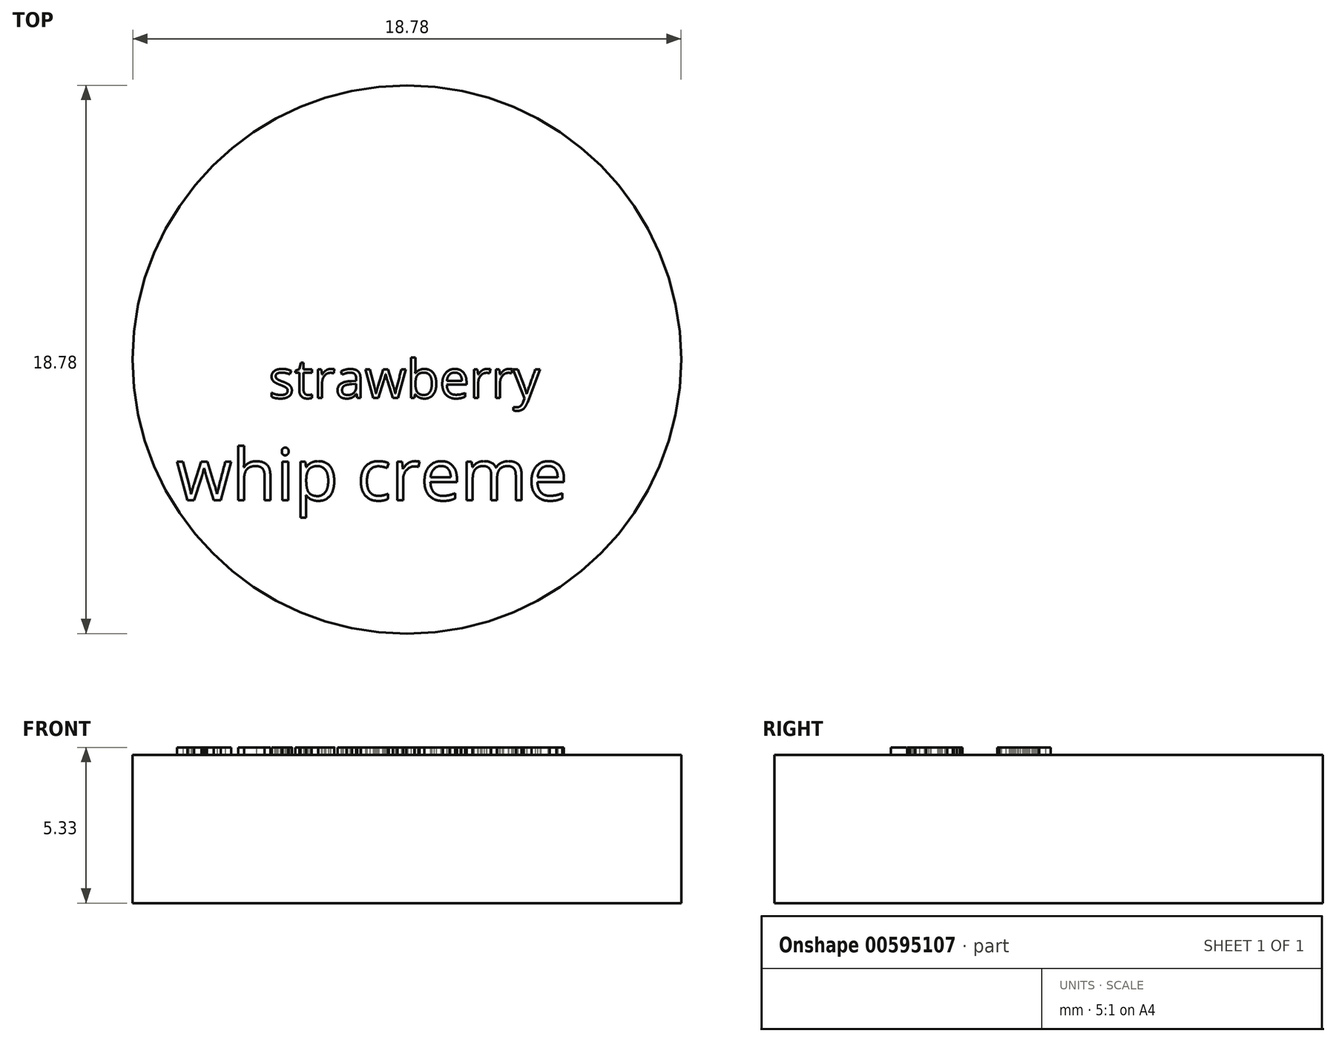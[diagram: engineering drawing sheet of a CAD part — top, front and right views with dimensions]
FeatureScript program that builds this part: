
annotation { "Feature Type Name" : "Feature", "Feature Type Description" : "" }
export const myFeature = defineFeature(function(context is Context, id is Id, definition is map)
    precondition{}
    {
        {
            var Q0;
            Q0=qCreatedBy(makeId("Top.planeOp"),FACE);
            var sketch = newSketch(context, id + "F0", { "sketchPlane" : qUnion([Q0])});
            skCircle(sketch, "E0", {"center": v(0, 0) * mm, "radius": 9.4 * mm});
            skSolve(sketch);
        }
        {
            var Q0;
            Q0=makeQuery(id+"F0.imprint","IMPRINT",FACE,{"disambiguationData":[TD([[makeQuery(id+"F0.imprint","IMPRINT",EDGE,{"derivedFrom":sQuery(id+"F0.wireOp",EDGE,"E0")}),1.0]])]});
            extrude(context, id + "F1", {"entities" : qUnion([Q0]), "oppositeDirection" : true, "depth" : 5.08 * mm, "offsetDistance" : 25.4 * mm});
        }
        {
            var Q0;
            Q0=makeQuery(id+"F1.opExtrude","CAP_FACE",FACE,{"disambiguationData":[OSD([sQuery(id+"F0.wireOp",EDGE,"E0")])],"isStart":true});
            var sketch = newSketch(context, id + "F2", { "sketchPlane" : qUnion([Q0])});
            skText(sketch, "E1", { "text": "strawberry", "fontName": "OpenSans-Regular.ttf"});
            const initialGuessF2  = {"E1": [-0.00473, -0.00132, 1, 0, 0.00132]};
            skSetInitialGuess(sketch, initialGuessF2);
            skSolve(sketch);
        }
        {
            var Q0;
            Q0=makeQuery(id+"F2.imprint","IMPRINT",FACE,{"disambiguationData":[TD([[makeQuery(id+"F2.imprint","IMPRINT",EDGE,{"derivedFrom":sQuery(id+"F2.wireOp",EDGE,"E1.sketch_text.stroke-0")}),1.0]])]});
            var sketch = newSketch(context, id + "F3", { "sketchPlane" : qUnion([Q0])});
            skText(sketch, "E2", { "text": "whip creme", "fontName": "OpenSans-Regular.ttf"});
            const initialGuessF3  = {"E2": [-0.0079, -0.00482, 1, 0, 0.00177]};
            skSetInitialGuess(sketch, initialGuessF3);
            skSolve(sketch);
        }
        {
            var Q0;
            Q0 = qSketchRegion(id + "F3", true);
            var Q1;
            Q1 = qSketchRegion(id + "F2", true);
            extrude(context, id + "F4", {"entities" : qUnion([Q0, Q1]), "operationType" : NewBodyOperationType.ADD, "depth" : 0.25 * mm, "offsetDistance" : 25.4 * mm});
        }
    });
